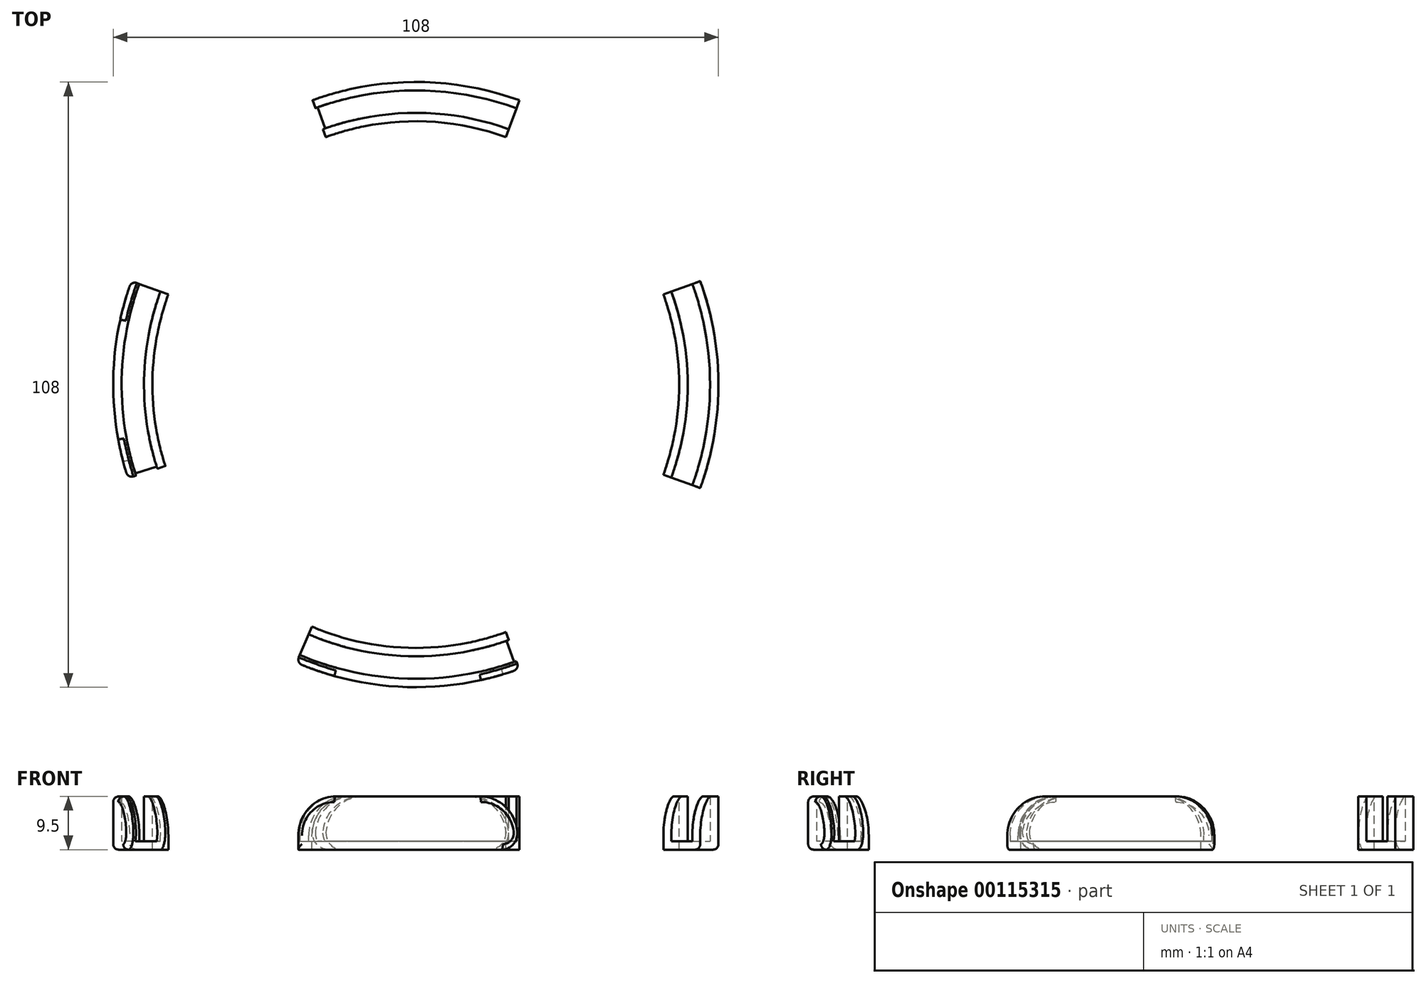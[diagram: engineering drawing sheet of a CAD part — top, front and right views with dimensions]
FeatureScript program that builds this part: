
annotation { "Feature Type Name" : "Feature", "Feature Type Description" : "" }
export const myFeature = defineFeature(function(context is Context, id is Id, definition is map)
    precondition{}
    {
        {
            var Q0;
            Q0=qCreatedBy(makeId("Top.planeOp"),FACE);
            var sketch = newSketch(context, id + "F0", { "sketchPlane" : qUnion([Q0])});
            skCircle(sketch, "E0", {"center": v(0, 0) * mm, "radius": 54 * mm});
            skSolve(sketch);
        }
        {
            var Q0;
            Q0 = qSketchRegion(id + "F0", true);
            extrude(context, id + "F1", {"entities" : qUnion([Q0]), "depth" : 9.5 * mm});
        }
        {
            var Q0;
            Q0=makeQuery(id+"F1.opExtrude","CAP_FACE",FACE,{"disambiguationData":[OSD([sQuery(id+"F0.wireOp",EDGE,"E0")])],"isStart":false});
            var sketch = newSketch(context, id + "F2", { "sketchPlane" : qUnion([Q0])});
            skCircle(sketch, "E1", {"center": v(0, 0) * mm, "radius": 48 * mm});
            skSolve(sketch);
        }
        {
            var Q0;
            Q0=sQuery(id+"F2.wireOp",VERTEX,"E1.center");
            var Q1;
            Q1=makeQuery(id+"F1.opExtrude","SWEPT_BODY",BODY,{"disambiguationData":[OSD([sQuery(id+"F0.wireOp",EDGE,"E0")])]});
            hole(context, id + "F3", {"style" : HoleStyle.SIMPLE, "endStyle" : HoleEndStyle.THROUGH, "holeDiameter" : 94 * mm, "locations" : qUnion([Q0]), "scope" : qUnion([Q1]), "isTappedThrough" : true});
        }
        {
            var Q0;
            Q0=makeQuery(id+"F1.opExtrude","CAP_FACE",FACE,{"disambiguationData":[OSD([sQuery(id+"F0.wireOp",EDGE,"E0")])],"isStart":false});
            shell(context, id + "F4", {"entities" : qUnion([Q0]), "thickness" : 1.5 * mm});
        }
        {
            var Q0;
            Q0=qCreatedBy(makeId("Top.planeOp"),FACE);
            var sketch = newSketch(context, id + "F5", { "sketchPlane" : qUnion([Q0])});
            skLineSegment(sketch, "E2", {"start": v(0, 0) * mm, "end": v(18.47, 50.74) * mm});
            skLineSegment(sketch, "E3", {"start": v(18.47, 50.74) * mm, "end": v(0, 0) * mm});
            skLineSegment(sketch, "E4", {"start": v(0, 0) * mm, "end": v(50.74, 18.47) * mm});
            skArc(sketch, "E5", {"start": v(50.74, 18.47) * mm, "mid": v(38.18, 38.18) * mm, "end": v(18.47, 50.74) * mm});
            skSolve(sketch);
        }
        {
            var Q0;
            Q0 = qSketchRegion(id + "F5", true);
            extrude(context, id + "F6", {"entities" : qUnion([Q0]), "operationType" : NewBodyOperationType.REMOVE, "depth" : 25 * mm});
        }
        {
            var Q0;
            Q0=qCreatedBy(makeId("Top.planeOp"),FACE);
            var sketch = newSketch(context, id + "F7", { "sketchPlane" : qUnion([Q0])});
            skLineSegment(sketch, "E6", {"start": v(0, 0) * mm, "end": v(-18.47, 50.74) * mm});
            skLineSegment(sketch, "E7", {"start": v(0, 0) * mm, "end": v(-50.74, 18.47) * mm});
            skArc(sketch, "E8", {"start": v(-18.47, 50.74) * mm, "mid": v(-38.18, 38.18) * mm, "end": v(-50.74, 18.47) * mm});
            skSolve(sketch);
        }
        {
            var Q0;
            Q0 = qSketchRegion(id + "F7", true);
            extrude(context, id + "F8", {"entities" : qUnion([Q0]), "operationType" : NewBodyOperationType.REMOVE, "depth" : 25 * mm});
        }
        {
            var Q0;
            Q0=qCreatedBy(makeId("Top.planeOp"),FACE);
            var sketch = newSketch(context, id + "F9", { "sketchPlane" : qUnion([Q0])});
            skLineSegment(sketch, "E9", {"start": v(50.74, -18.47) * mm, "end": v(0, 0) * mm});
            skLineSegment(sketch, "E10", {"start": v(0, 0) * mm, "end": v(18.47, -50.74) * mm});
            skArc(sketch, "E11", {"start": v(18.47, -50.74) * mm, "mid": v(38.18, -38.18) * mm, "end": v(50.74, -18.47) * mm});
            skSolve(sketch);
        }
        {
            var Q0;
            Q0 = qSketchRegion(id + "F9", true);
            extrude(context, id + "F10", {"entities" : qUnion([Q0]), "operationType" : NewBodyOperationType.REMOVE, "depth" : 25 * mm});
        }
        {
            var Q0;
            Q0=qCreatedBy(makeId("Top.planeOp"),FACE);
            var sketch = newSketch(context, id + "F11", { "sketchPlane" : qUnion([Q0])});
            skLineSegment(sketch, "E12", {"start": v(0, 0) * mm, "end": v(-21.28, -49.63) * mm});
            skLineSegment(sketch, "E13", {"start": v(0, 0) * mm, "end": v(-51.34, -16.72) * mm});
            skArc(sketch, "E14", {"start": v(-51.34, -16.72) * mm, "mid": v(-39.87, -36.42) * mm, "end": v(-21.28, -49.63) * mm});
            skSolve(sketch);
        }
        {
            var Q0;
            Q0 = qSketchRegion(id + "F11", true);
            extrude(context, id + "F12", {"entities" : qUnion([Q0]), "operationType" : NewBodyOperationType.REMOVE, "depth" : 25 * mm});
        }
        {
            var Q0;
            {var subQ0=sQuery(id+"F0.wireOp",EDGE,"E0");Q0=makeQuery(id+"F6.boolean.opBoolean","INTERSECT",EDGE,{"derivedFrom":[makeQuery(id+"F4.opShell","OFFSET_FACE",FACE,{"disambiguationData":[OSD([subQ0]),TDD([makeQuery(id+"F1.opExtrude","CAP_FACE",FACE,{"disambiguationData":[OSD([subQ0])],"isStart":false})])]}),makeQuery(id+"F6.opExtrude","SWEPT_FACE",FACE,{"disambiguationData":[OSD([sQuery(id+"F5.wireOp",EDGE,"E4")])]})]});}
            var Q1;
            {var subQ1=sQuery(id+"F0.wireOp",EDGE,"E0");Q1=makeQuery(id+"F10.boolean.opBoolean","INTERSECT",EDGE,{"derivedFrom":[makeQuery(id+"F8.boolean.opBoolean","SPLIT",FACE,{"disambiguationData":[TD([makeQuery(id+"F6.boolean.opBoolean","COPY",FACE,{"derivedFrom":makeQuery(id+"F6.opExtrude","SWEPT_FACE",FACE,{"disambiguationData":[OSD([sQuery(id+"F5.wireOp",EDGE,"E4")])]})})])],"derivedFrom":makeQuery(id+"F4.opShell","OFFSET_FACE",FACE,{"disambiguationData":[OSD([subQ1]),TDD([makeQuery(id+"F1.opExtrude","CAP_FACE",FACE,{"disambiguationData":[OSD([subQ1])],"isStart":false})])]})}),makeQuery(id+"F10.opExtrude","SWEPT_FACE",FACE,{"disambiguationData":[OSD([sQuery(id+"F9.wireOp",EDGE,"E9")])]})]});}
            var Q2;
            {var subQ0=sQuery(id+"F0.wireOp",EDGE,"E0");Q2=makeQuery(id+"F10.boolean.opBoolean","INTERSECT",EDGE,{"derivedFrom":[makeQuery(id+"F8.boolean.opBoolean","SPLIT",FACE,{"disambiguationData":[TD([makeQuery(id+"F6.boolean.opBoolean","COPY",FACE,{"derivedFrom":makeQuery(id+"F6.opExtrude","SWEPT_FACE",FACE,{"disambiguationData":[OSD([sQuery(id+"F5.wireOp",EDGE,"E4")])]})})])],"derivedFrom":makeQuery(id+"F1.opExtrude","CAP_FACE",FACE,{"disambiguationData":[OSD([subQ0])],"isStart":false})}),makeQuery(id+"F10.opExtrude","SWEPT_FACE",FACE,{"disambiguationData":[OSD([sQuery(id+"F9.wireOp",EDGE,"E9")])]})]});}
            var Q3;
            Q3=makeQuery(id+"F6.boolean.opBoolean","INTERSECT",EDGE,{"derivedFrom":[makeQuery(id+"F1.opExtrude","CAP_FACE",FACE,{"disambiguationData":[OSD([sQuery(id+"F0.wireOp",EDGE,"E0")])],"isStart":false}),makeQuery(id+"F6.opExtrude","SWEPT_FACE",FACE,{"disambiguationData":[OSD([sQuery(id+"F5.wireOp",EDGE,"E4")])]})]});
            var Q4;
            {var subQ0=sQuery(id+"F0.wireOp",EDGE,"E0");var subQ3=makeQuery(id+"F8.opExtrude","SWEPT_FACE",FACE,{"disambiguationData":[OSD([sQuery(id+"F7.wireOp",EDGE,"E7")])]});Q4=makeQuery(id+"F12.boolean.opBoolean","INTERSECT",EDGE,{"derivedFrom":[makeQuery(id+"F10.boolean.opBoolean","SPLIT",FACE,{"disambiguationData":[TD([makeQuery(id+"F8.boolean.opBoolean","COPY",FACE,{"derivedFrom":subQ3})])],"derivedFrom":makeQuery(id+"F8.boolean.opBoolean","SPLIT",FACE,{"disambiguationData":[TD([makeQuery(id+"F6.boolean.opBoolean","COPY",FACE,{"derivedFrom":makeQuery(id+"F6.opExtrude","SWEPT_FACE",FACE,{"disambiguationData":[OSD([sQuery(id+"F5.wireOp",EDGE,"E4")])]})})])],"derivedFrom":makeQuery(id+"F1.opExtrude","CAP_FACE",FACE,{"disambiguationData":[OSD([subQ0])],"isStart":false})})}),makeQuery(id+"F12.opExtrude","SWEPT_FACE",FACE,{"disambiguationData":[OSD([sQuery(id+"F11.wireOp",EDGE,"E12")])]})]});}
            var Q5;
            {var subQ3=makeQuery(id+"F8.opExtrude","SWEPT_FACE",FACE,{"disambiguationData":[OSD([sQuery(id+"F7.wireOp",EDGE,"E7")])]});var subQ4=sQuery(id+"F0.wireOp",EDGE,"E0");Q5=makeQuery(id+"F12.boolean.opBoolean","INTERSECT",EDGE,{"derivedFrom":[makeQuery(id+"F10.boolean.opBoolean","SPLIT",FACE,{"disambiguationData":[TD([makeQuery(id+"F8.boolean.opBoolean","COPY",FACE,{"derivedFrom":subQ3})])],"derivedFrom":makeQuery(id+"F8.boolean.opBoolean","SPLIT",FACE,{"disambiguationData":[TD([makeQuery(id+"F6.boolean.opBoolean","COPY",FACE,{"derivedFrom":makeQuery(id+"F6.opExtrude","SWEPT_FACE",FACE,{"disambiguationData":[OSD([sQuery(id+"F5.wireOp",EDGE,"E4")])]})})])],"derivedFrom":makeQuery(id+"F4.opShell","OFFSET_FACE",FACE,{"disambiguationData":[OSD([subQ4]),TDD([makeQuery(id+"F1.opExtrude","CAP_FACE",FACE,{"disambiguationData":[OSD([subQ4])],"isStart":false})])]})})}),makeQuery(id+"F12.opExtrude","SWEPT_FACE",FACE,{"disambiguationData":[OSD([sQuery(id+"F11.wireOp",EDGE,"E12")])]})]});}
            var Q6;
            {var subQ1=sQuery(id+"F0.wireOp",EDGE,"E0");Q6=makeQuery(id+"F10.boolean.opBoolean","INTERSECT",EDGE,{"derivedFrom":[makeQuery(id+"F8.boolean.opBoolean","SPLIT",FACE,{"disambiguationData":[TD([makeQuery(id+"F6.boolean.opBoolean","COPY",FACE,{"derivedFrom":makeQuery(id+"F6.opExtrude","SWEPT_FACE",FACE,{"disambiguationData":[OSD([sQuery(id+"F5.wireOp",EDGE,"E4")])]})})])],"derivedFrom":makeQuery(id+"F4.opShell","OFFSET_FACE",FACE,{"disambiguationData":[OSD([subQ1]),TDD([makeQuery(id+"F1.opExtrude","CAP_FACE",FACE,{"disambiguationData":[OSD([subQ1])],"isStart":false})])]})}),makeQuery(id+"F10.opExtrude","SWEPT_FACE",FACE,{"disambiguationData":[OSD([sQuery(id+"F9.wireOp",EDGE,"E10")])]})]});}
            var Q7;
            {var subQ0=sQuery(id+"F0.wireOp",EDGE,"E0");Q7=makeQuery(id+"F10.boolean.opBoolean","INTERSECT",EDGE,{"derivedFrom":[makeQuery(id+"F8.boolean.opBoolean","SPLIT",FACE,{"disambiguationData":[TD([makeQuery(id+"F6.boolean.opBoolean","COPY",FACE,{"derivedFrom":makeQuery(id+"F6.opExtrude","SWEPT_FACE",FACE,{"disambiguationData":[OSD([sQuery(id+"F5.wireOp",EDGE,"E4")])]})})])],"derivedFrom":makeQuery(id+"F1.opExtrude","CAP_FACE",FACE,{"disambiguationData":[OSD([subQ0])],"isStart":false})}),makeQuery(id+"F10.opExtrude","SWEPT_FACE",FACE,{"disambiguationData":[OSD([sQuery(id+"F9.wireOp",EDGE,"E10")])]})]});}
            var Q8;
            {var subQ3=makeQuery(id+"F8.opExtrude","SWEPT_FACE",FACE,{"disambiguationData":[OSD([sQuery(id+"F7.wireOp",EDGE,"E7")])]});var subQ4=sQuery(id+"F0.wireOp",EDGE,"E0");Q8=makeQuery(id+"F12.boolean.opBoolean","INTERSECT",EDGE,{"derivedFrom":[makeQuery(id+"F10.boolean.opBoolean","SPLIT",FACE,{"disambiguationData":[TD([makeQuery(id+"F8.boolean.opBoolean","COPY",FACE,{"derivedFrom":subQ3})])],"derivedFrom":makeQuery(id+"F8.boolean.opBoolean","SPLIT",FACE,{"disambiguationData":[TD([makeQuery(id+"F6.boolean.opBoolean","COPY",FACE,{"derivedFrom":makeQuery(id+"F6.opExtrude","SWEPT_FACE",FACE,{"disambiguationData":[OSD([sQuery(id+"F5.wireOp",EDGE,"E4")])]})})])],"derivedFrom":makeQuery(id+"F4.opShell","OFFSET_FACE",FACE,{"disambiguationData":[OSD([subQ4]),TDD([makeQuery(id+"F1.opExtrude","CAP_FACE",FACE,{"disambiguationData":[OSD([subQ4])],"isStart":false})])]})})}),makeQuery(id+"F12.opExtrude","SWEPT_FACE",FACE,{"disambiguationData":[OSD([sQuery(id+"F11.wireOp",EDGE,"E13")])]})]});}
            var Q9;
            {var subQ0=sQuery(id+"F0.wireOp",EDGE,"E0");var subQ3=makeQuery(id+"F8.opExtrude","SWEPT_FACE",FACE,{"disambiguationData":[OSD([sQuery(id+"F7.wireOp",EDGE,"E7")])]});Q9=makeQuery(id+"F12.boolean.opBoolean","INTERSECT",EDGE,{"derivedFrom":[makeQuery(id+"F10.boolean.opBoolean","SPLIT",FACE,{"disambiguationData":[TD([makeQuery(id+"F8.boolean.opBoolean","COPY",FACE,{"derivedFrom":subQ3})])],"derivedFrom":makeQuery(id+"F8.boolean.opBoolean","SPLIT",FACE,{"disambiguationData":[TD([makeQuery(id+"F6.boolean.opBoolean","COPY",FACE,{"derivedFrom":makeQuery(id+"F6.opExtrude","SWEPT_FACE",FACE,{"disambiguationData":[OSD([sQuery(id+"F5.wireOp",EDGE,"E4")])]})})])],"derivedFrom":makeQuery(id+"F1.opExtrude","CAP_FACE",FACE,{"disambiguationData":[OSD([subQ0])],"isStart":false})})}),makeQuery(id+"F12.opExtrude","SWEPT_FACE",FACE,{"disambiguationData":[OSD([sQuery(id+"F11.wireOp",EDGE,"E13")])]})]});}
            var Q10;
            {var subQ0=sQuery(id+"F0.wireOp",EDGE,"E0");Q10=makeQuery(id+"F8.boolean.opBoolean","INTERSECT",EDGE,{"derivedFrom":[makeQuery(id+"F4.opShell","OFFSET_FACE",FACE,{"disambiguationData":[OSD([subQ0]),TDD([makeQuery(id+"F1.opExtrude","CAP_FACE",FACE,{"disambiguationData":[OSD([subQ0])],"isStart":false})])]}),makeQuery(id+"F8.opExtrude","SWEPT_FACE",FACE,{"disambiguationData":[OSD([sQuery(id+"F7.wireOp",EDGE,"E6")])]})]});}
            var Q11;
            {var subQ0=sQuery(id+"F0.wireOp",EDGE,"E0");Q11=makeQuery(id+"F6.boolean.opBoolean","INTERSECT",EDGE,{"derivedFrom":[makeQuery(id+"F4.opShell","OFFSET_FACE",FACE,{"disambiguationData":[OSD([subQ0]),TDD([makeQuery(id+"F1.opExtrude","CAP_FACE",FACE,{"disambiguationData":[OSD([subQ0])],"isStart":false})])]}),makeQuery(id+"F6.opExtrude","SWEPT_FACE",FACE,{"disambiguationData":[OSD([sQuery(id+"F5.wireOp",EDGE,"E3")])]})]});}
            var Q12;
            {var subQ0=sQuery(id+"F0.wireOp",EDGE,"E0");Q12=makeQuery(id+"F8.boolean.opBoolean","INTERSECT",EDGE,{"derivedFrom":[makeQuery(id+"F4.opShell","OFFSET_FACE",FACE,{"disambiguationData":[OSD([subQ0]),TDD([makeQuery(id+"F1.opExtrude","CAP_FACE",FACE,{"disambiguationData":[OSD([subQ0])],"isStart":false})])]}),makeQuery(id+"F8.opExtrude","SWEPT_FACE",FACE,{"disambiguationData":[OSD([sQuery(id+"F7.wireOp",EDGE,"E7")])]})]});}
            var Q13;
            Q13=makeQuery(id+"F8.boolean.opBoolean","INTERSECT",EDGE,{"derivedFrom":[makeQuery(id+"F1.opExtrude","CAP_FACE",FACE,{"disambiguationData":[OSD([sQuery(id+"F0.wireOp",EDGE,"E0")])],"isStart":false}),makeQuery(id+"F8.opExtrude","SWEPT_FACE",FACE,{"disambiguationData":[OSD([sQuery(id+"F7.wireOp",EDGE,"E7")])]})]});
            var Q14;
            Q14=makeQuery(id+"F8.boolean.opBoolean","INTERSECT",EDGE,{"derivedFrom":[makeQuery(id+"F1.opExtrude","CAP_FACE",FACE,{"disambiguationData":[OSD([sQuery(id+"F0.wireOp",EDGE,"E0")])],"isStart":false}),makeQuery(id+"F8.opExtrude","SWEPT_FACE",FACE,{"disambiguationData":[OSD([sQuery(id+"F7.wireOp",EDGE,"E6")])]})]});
            var Q15;
            Q15=makeQuery(id+"F6.boolean.opBoolean","INTERSECT",EDGE,{"derivedFrom":[makeQuery(id+"F1.opExtrude","CAP_FACE",FACE,{"disambiguationData":[OSD([sQuery(id+"F0.wireOp",EDGE,"E0")])],"isStart":false}),makeQuery(id+"F6.opExtrude","SWEPT_FACE",FACE,{"disambiguationData":[OSD([sQuery(id+"F5.wireOp",EDGE,"E3")])]})]});
            fillet(context, id + "F13", {"entities" : qUnion([Q0, Q1, Q2, Q3, Q4, Q5, Q6, Q7, Q8, Q9, Q10, Q11, Q12, Q13, Q14, Q15]), "radius" : 7 * mm, "tangentPropagation" : true, "allowEdgeOverflow" : false});
        }
        {
            var Q0;
            Q0=makeQuery(id+"F6.boolean.opBoolean","COPY",EDGE,{"derivedFrom":makeQuery(id+"F6.opExtrude","CAP_EDGE",EDGE,{"disambiguationData":[OSD([sQuery(id+"F5.wireOp",EDGE,"E4")])],"isStart":true})});
            var Q1;
            Q1=makeQuery(id+"F10.boolean.opBoolean","COPY",EDGE,{"derivedFrom":makeQuery(id+"F10.opExtrude","CAP_EDGE",EDGE,{"disambiguationData":[OSD([sQuery(id+"F9.wireOp",EDGE,"E9")])],"isStart":true})});
            var Q2;
            Q2=makeQuery(id+"F10.boolean.opBoolean","COPY",EDGE,{"derivedFrom":makeQuery(id+"F10.opExtrude","CAP_EDGE",EDGE,{"disambiguationData":[OSD([sQuery(id+"F9.wireOp",EDGE,"E10")])],"isStart":true})});
            var Q3;
            Q3=makeQuery(id+"F12.boolean.opBoolean","COPY",EDGE,{"derivedFrom":makeQuery(id+"F12.opExtrude","CAP_EDGE",EDGE,{"disambiguationData":[OSD([sQuery(id+"F11.wireOp",EDGE,"E12")])],"isStart":true})});
            var Q4;
            Q4=makeQuery(id+"F12.boolean.opBoolean","COPY",EDGE,{"derivedFrom":makeQuery(id+"F12.opExtrude","CAP_EDGE",EDGE,{"disambiguationData":[OSD([sQuery(id+"F11.wireOp",EDGE,"E13")])],"isStart":true})});
            var Q5;
            Q5=makeQuery(id+"F8.boolean.opBoolean","COPY",EDGE,{"derivedFrom":makeQuery(id+"F8.opExtrude","CAP_EDGE",EDGE,{"disambiguationData":[OSD([sQuery(id+"F7.wireOp",EDGE,"E7")])],"isStart":true})});
            var Q6;
            Q6=makeQuery(id+"F8.boolean.opBoolean","COPY",EDGE,{"derivedFrom":makeQuery(id+"F8.opExtrude","CAP_EDGE",EDGE,{"disambiguationData":[OSD([sQuery(id+"F7.wireOp",EDGE,"E6")])],"isStart":true})});
            var Q7;
            Q7=makeQuery(id+"F6.boolean.opBoolean","COPY",EDGE,{"derivedFrom":makeQuery(id+"F6.opExtrude","CAP_EDGE",EDGE,{"disambiguationData":[OSD([sQuery(id+"F5.wireOp",EDGE,"E3")])],"isStart":true})});
            fillet(context, id + "F14", {"entities" : qUnion([Q0, Q1, Q2, Q3, Q4, Q5, Q6, Q7]), "radius" : 3 * mm, "tangentPropagation" : true, "allowEdgeOverflow" : false});
        }
        {
            var Q0;
            {var subQ0=sQuery(id+"F0.wireOp",EDGE,"E0");var subQ3=makeQuery(id+"F8.opExtrude","SWEPT_FACE",FACE,{"disambiguationData":[OSD([sQuery(id+"F7.wireOp",EDGE,"E7")])]});var subQ4=makeQuery(id+"F8.boolean.opBoolean","COPY",FACE,{"derivedFrom":subQ3});Q0=makeQuery(id+"F12.boolean.opBoolean","SPLIT",EDGE,{"disambiguationData":[TD([subQ4])],"derivedFrom":makeQuery(id+"F10.boolean.opBoolean","SPLIT",EDGE,{"disambiguationData":[TD([subQ4])],"derivedFrom":makeQuery(id+"F8.boolean.opBoolean","SPLIT",EDGE,{"disambiguationData":[TD([makeQuery(id+"F6.boolean.opBoolean","COPY",FACE,{"derivedFrom":makeQuery(id+"F6.opExtrude","SWEPT_FACE",FACE,{"disambiguationData":[OSD([sQuery(id+"F5.wireOp",EDGE,"E4")])]})})])],"derivedFrom":makeQuery(id+"F1.opExtrude","CAP_EDGE",EDGE,{"disambiguationData":[OSD([subQ0])],"isStart":true})})})});}
            var Q1;
            {var subQ0=makeQuery(id+"F1.opExtrude","CAP_FACE",FACE,{"disambiguationData":[OSD([sQuery(id+"F0.wireOp",EDGE,"E0")])],"isStart":true});var subQ1=makeQuery(id+"F3.hole-0.opRevolve","SWEPT_FACE",FACE,{"disambiguationData":[OSD([sQuery(id+"F3.hole-0.sketch.wireOp",EDGE,"core_line_2")])]});var subQ3=makeQuery(id+"F8.opExtrude","SWEPT_FACE",FACE,{"disambiguationData":[OSD([sQuery(id+"F7.wireOp",EDGE,"E7")])]});var subQ4=makeQuery(id+"F8.boolean.opBoolean","COPY",FACE,{"derivedFrom":subQ3});Q1=makeQuery(id+"F12.boolean.opBoolean","SPLIT",EDGE,{"disambiguationData":[TD([subQ4])],"derivedFrom":makeQuery(id+"F10.boolean.opBoolean","SPLIT",EDGE,{"disambiguationData":[TD([subQ4])],"derivedFrom":makeQuery(id+"F8.boolean.opBoolean","SPLIT",EDGE,{"disambiguationData":[TD([makeQuery(id+"F6.boolean.opBoolean","COPY",FACE,{"derivedFrom":makeQuery(id+"F6.opExtrude","SWEPT_FACE",FACE,{"disambiguationData":[OSD([sQuery(id+"F5.wireOp",EDGE,"E4")])]})})])],"derivedFrom":makeQuery(id+"F3.hole-0.boolean.opBoolean","INTERSECT",EDGE,{"derivedFrom":[subQ0,subQ1]})})})});}
            var Q2;
            {var subQ0=makeQuery(id+"F1.opExtrude","CAP_FACE",FACE,{"disambiguationData":[OSD([sQuery(id+"F0.wireOp",EDGE,"E0")])],"isStart":true});var subQ1=makeQuery(id+"F3.hole-0.opRevolve","SWEPT_FACE",FACE,{"disambiguationData":[OSD([sQuery(id+"F3.hole-0.sketch.wireOp",EDGE,"core_line_2")])]});var subQ3=makeQuery(id+"F10.opExtrude","SWEPT_FACE",FACE,{"disambiguationData":[OSD([sQuery(id+"F9.wireOp",EDGE,"E10")])]});var subQ4=makeQuery(id+"F8.opExtrude","SWEPT_FACE",FACE,{"disambiguationData":[OSD([sQuery(id+"F7.wireOp",EDGE,"E7")])]});Q2=makeQuery(id+"F12.boolean.opBoolean","SPLIT",EDGE,{"disambiguationData":[TD([makeQuery(id+"F10.boolean.opBoolean","COPY",FACE,{"derivedFrom":subQ3})])],"derivedFrom":makeQuery(id+"F10.boolean.opBoolean","SPLIT",EDGE,{"disambiguationData":[TD([makeQuery(id+"F8.boolean.opBoolean","COPY",FACE,{"derivedFrom":subQ4})])],"derivedFrom":makeQuery(id+"F8.boolean.opBoolean","SPLIT",EDGE,{"disambiguationData":[TD([makeQuery(id+"F6.boolean.opBoolean","COPY",FACE,{"derivedFrom":makeQuery(id+"F6.opExtrude","SWEPT_FACE",FACE,{"disambiguationData":[OSD([sQuery(id+"F5.wireOp",EDGE,"E4")])]})})])],"derivedFrom":makeQuery(id+"F3.hole-0.boolean.opBoolean","INTERSECT",EDGE,{"derivedFrom":[subQ0,subQ1]})})})});}
            var Q3;
            {var subQ0=sQuery(id+"F0.wireOp",EDGE,"E0");var subQ3=makeQuery(id+"F10.opExtrude","SWEPT_FACE",FACE,{"disambiguationData":[OSD([sQuery(id+"F9.wireOp",EDGE,"E10")])]});var subQ4=makeQuery(id+"F8.opExtrude","SWEPT_FACE",FACE,{"disambiguationData":[OSD([sQuery(id+"F7.wireOp",EDGE,"E7")])]});Q3=makeQuery(id+"F12.boolean.opBoolean","SPLIT",EDGE,{"disambiguationData":[TD([makeQuery(id+"F10.boolean.opBoolean","COPY",FACE,{"derivedFrom":subQ3})])],"derivedFrom":makeQuery(id+"F10.boolean.opBoolean","SPLIT",EDGE,{"disambiguationData":[TD([makeQuery(id+"F8.boolean.opBoolean","COPY",FACE,{"derivedFrom":subQ4})])],"derivedFrom":makeQuery(id+"F8.boolean.opBoolean","SPLIT",EDGE,{"disambiguationData":[TD([makeQuery(id+"F6.boolean.opBoolean","COPY",FACE,{"derivedFrom":makeQuery(id+"F6.opExtrude","SWEPT_FACE",FACE,{"disambiguationData":[OSD([sQuery(id+"F5.wireOp",EDGE,"E4")])]})})])],"derivedFrom":makeQuery(id+"F1.opExtrude","CAP_EDGE",EDGE,{"disambiguationData":[OSD([subQ0])],"isStart":true})})})});}
            var Q4;
            {var subQ0=sQuery(id+"F0.wireOp",EDGE,"E0");var subQ3=makeQuery(id+"F6.boolean.opBoolean","COPY",FACE,{"derivedFrom":makeQuery(id+"F6.opExtrude","SWEPT_FACE",FACE,{"disambiguationData":[OSD([sQuery(id+"F5.wireOp",EDGE,"E4")])]})});Q4=makeQuery(id+"F10.boolean.opBoolean","SPLIT",EDGE,{"disambiguationData":[TD([subQ3])],"derivedFrom":makeQuery(id+"F8.boolean.opBoolean","SPLIT",EDGE,{"disambiguationData":[TD([subQ3])],"derivedFrom":makeQuery(id+"F1.opExtrude","CAP_EDGE",EDGE,{"disambiguationData":[OSD([subQ0])],"isStart":true})})});}
            var Q5;
            {var subQ0=makeQuery(id+"F1.opExtrude","CAP_FACE",FACE,{"disambiguationData":[OSD([sQuery(id+"F0.wireOp",EDGE,"E0")])],"isStart":true});var subQ1=makeQuery(id+"F3.hole-0.opRevolve","SWEPT_FACE",FACE,{"disambiguationData":[OSD([sQuery(id+"F3.hole-0.sketch.wireOp",EDGE,"core_line_2")])]});var subQ3=makeQuery(id+"F6.boolean.opBoolean","COPY",FACE,{"derivedFrom":makeQuery(id+"F6.opExtrude","SWEPT_FACE",FACE,{"disambiguationData":[OSD([sQuery(id+"F5.wireOp",EDGE,"E4")])]})});Q5=makeQuery(id+"F10.boolean.opBoolean","SPLIT",EDGE,{"disambiguationData":[TD([subQ3])],"derivedFrom":makeQuery(id+"F8.boolean.opBoolean","SPLIT",EDGE,{"disambiguationData":[TD([subQ3])],"derivedFrom":makeQuery(id+"F3.hole-0.boolean.opBoolean","INTERSECT",EDGE,{"derivedFrom":[subQ0,subQ1]})})});}
            var Q6;
            {var subQ0=sQuery(id+"F0.wireOp",EDGE,"E0");Q6=makeQuery(id+"F8.boolean.opBoolean","SPLIT",EDGE,{"disambiguationData":[TD([makeQuery(id+"F6.boolean.opBoolean","COPY",FACE,{"derivedFrom":makeQuery(id+"F6.opExtrude","SWEPT_FACE",FACE,{"disambiguationData":[OSD([sQuery(id+"F5.wireOp",EDGE,"E3")])]})})])],"derivedFrom":makeQuery(id+"F1.opExtrude","CAP_EDGE",EDGE,{"disambiguationData":[OSD([subQ0])],"isStart":true})});}
            var Q7;
            {var subQ0=makeQuery(id+"F1.opExtrude","CAP_FACE",FACE,{"disambiguationData":[OSD([sQuery(id+"F0.wireOp",EDGE,"E0")])],"isStart":true});var subQ1=makeQuery(id+"F3.hole-0.opRevolve","SWEPT_FACE",FACE,{"disambiguationData":[OSD([sQuery(id+"F3.hole-0.sketch.wireOp",EDGE,"core_line_2")])]});Q7=makeQuery(id+"F8.boolean.opBoolean","SPLIT",EDGE,{"disambiguationData":[TD([makeQuery(id+"F6.boolean.opBoolean","COPY",FACE,{"derivedFrom":makeQuery(id+"F6.opExtrude","SWEPT_FACE",FACE,{"disambiguationData":[OSD([sQuery(id+"F5.wireOp",EDGE,"E3")])]})})])],"derivedFrom":makeQuery(id+"F3.hole-0.boolean.opBoolean","INTERSECT",EDGE,{"derivedFrom":[subQ0,subQ1]})});}
            fillet(context, id + "F15", {"entities" : qUnion([Q0, Q1, Q2, Q3, Q4, Q5, Q6, Q7]), "radius" : 1 * mm, "tangentPropagation" : true, "allowEdgeOverflow" : false});
        }
    });
